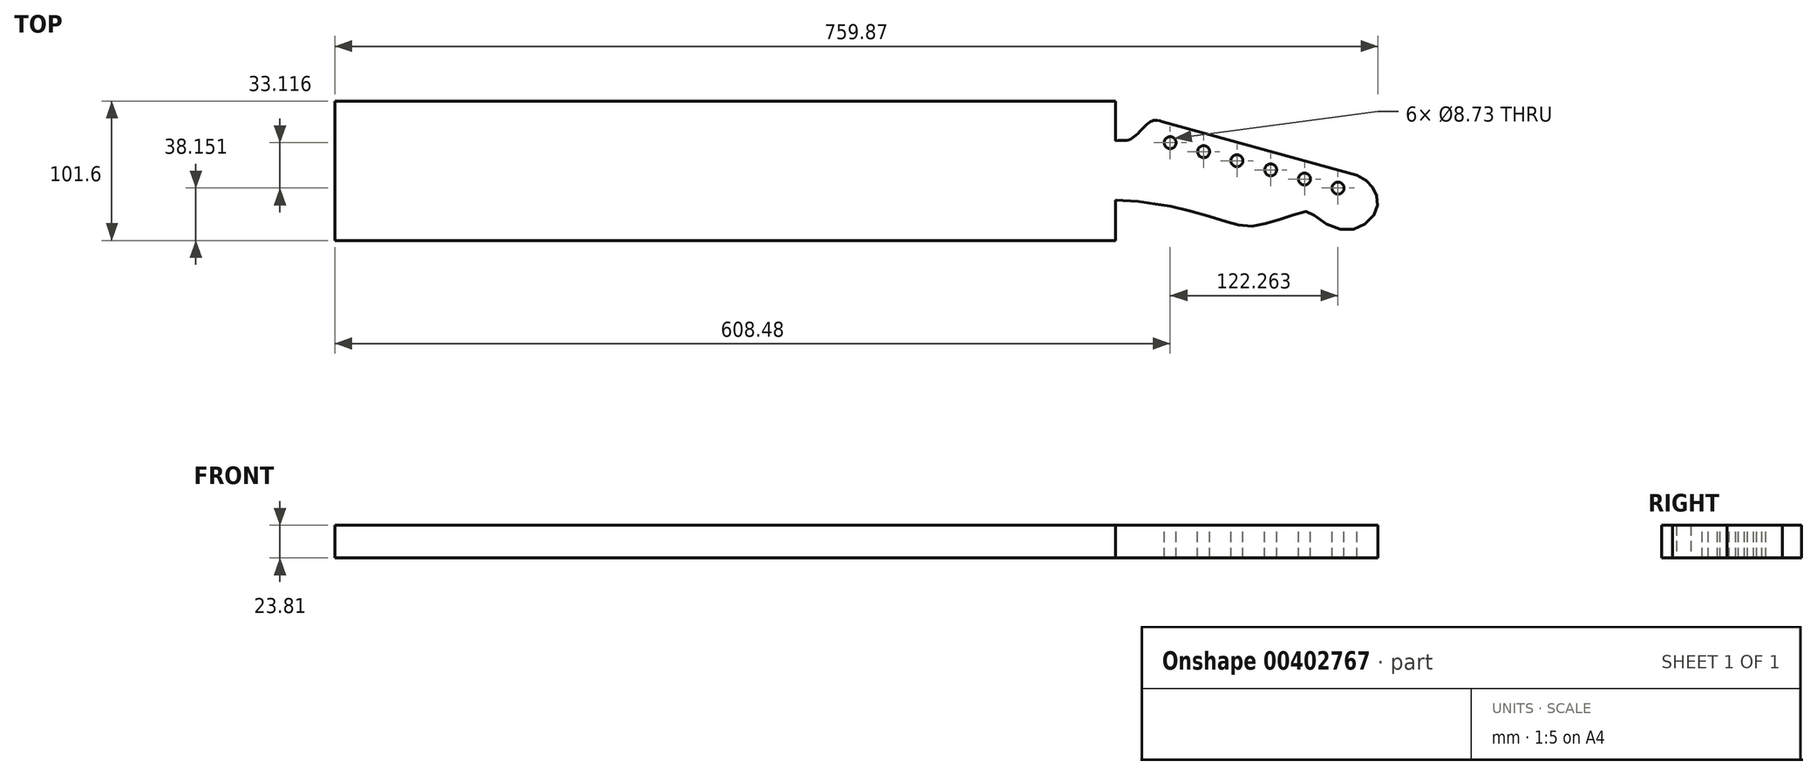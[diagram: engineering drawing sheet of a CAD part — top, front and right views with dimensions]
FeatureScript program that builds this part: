
annotation { "Feature Type Name" : "Feature", "Feature Type Description" : "" }
export const myFeature = defineFeature(function(context is Context, id is Id, definition is map)
    precondition{}
    {
        {
            var Q0;
            Q0=qCreatedBy(makeId("Top.planeOp"),FACE);
            var sketch = newSketch(context, id + "F0", { "sketchPlane" : qUnion([Q0])});
            skLineSegment(sketch, "E0", {"start": v(-323.85, 0) * mm, "end": v(323.85, 0) * mm, "construction": true});
            skLineSegment(sketch, "E1", {"start": v(323.85, 21.43) * mm, "end": v(323.85, -21.43) * mm, "construction": true});
            skLineSegment(sketch, "E2", {"start": v(323.85, 0) * mm, "end": v(327.03, 0) * mm, "construction": true});
            skLineSegment(sketch, "E3", {"start": v(327.03, 21.43) * mm, "end": v(327.03, -21.43) * mm, "construction": true});
            skSolve(sketch);
        }
        {
            var Q0;
            Q0=qCreatedBy(makeId("Top.planeOp"),FACE);
            var sketch = newSketch(context, id + "F1", { "sketchPlane" : qUnion([Q0])});
            skLineSegment(sketch, "E4.bottom", {"start": v(520.42, 50.8) * mm, "end": v(-241.58, 50.8) * mm});
            skLineSegment(sketch, "E4.top", {"start": v(520.42, -50.8) * mm, "end": v(-241.58, -50.8) * mm});
            skLineSegment(sketch, "E4.left", {"start": v(520.42, 50.8) * mm, "end": v(520.42, -50.8) * mm});
            skLineSegment(sketch, "E4.right", {"start": v(-241.58, 50.8) * mm, "end": v(-241.58, -50.8) * mm});
            skPoint(sketch, "E5", {"position": v(520.42, 0) * mm});
            skSolve(sketch);
        }
        {
            var Q0;
            Q0 = qSketchRegion(id + "F1", true);
            extrude(context, id + "F2", {"entities" : qUnion([Q0]), "oppositeDirection" : true, "depth" : 23.8 * mm});
        }
        {
            var Q0;
            Q0=qCreatedBy(makeId("Top.planeOp"),FACE);
            var sketch = newSketch(context, id + "F3", { "sketchPlane" : qUnion([Q0])});
            skLineSegment(sketch, "E6", {"start": v(325.44, 21.43) * mm, "end": v(325.44, -21.43) * mm});
            skCircle(sketch, "E7", {"center": v(366.9, 20.47) * mm, "radius": 4.37 * mm});
            skPoint(sketch, "E8", {"position": v(325.44, 0) * mm});
            skLineSegment(sketch, "E9", {"start": v(-178.02, 0) * mm, "end": v(520.42, 0) * mm, "construction": true});
            skPoint(sketch, "E10", {"position": v(361.08, 35.86) * mm});
            skPoint(sketch, "E11", {"position": v(503.05, -3.23) * mm});
            skLineSegment(sketch, "E12", {"start": v(361.08, 35.86) * mm, "end": v(503.05, -3.23) * mm});
            skCircle(sketch, "E13", {"center": v(489.16, -12.65) * mm, "radius": 4.37 * mm});
            skLineSegment(sketch, "E14", {"start": v(366.9, 20.47) * mm, "end": v(489.16, -12.65) * mm, "construction": true});
            skCircle(sketch, "E15", {"center": v(464.73, -6.03) * mm, "radius": 4.37 * mm});
            skCircle(sketch, "E16", {"center": v(440.11, 0.64) * mm, "radius": 4.37 * mm});
            skCircle(sketch, "E17", {"center": v(415.53, 7.3) * mm, "radius": 4.37 * mm});
            skCircle(sketch, "E18", {"center": v(391.26, 13.87) * mm, "radius": 4.37 * mm});
            skFitSpline(sketch, "E19", {"points": [v(325.44, 21.43) * mm, v(327.1, 21.9) * mm, v(333.07, 22.03) * mm, v(336.36, 22.34) * mm, v(339.35, 23.78) * mm, v(341.85, 25.84) * mm, v(345.43, 29.07) * mm, v(348.04, 31.8) * mm, v(350.96, 34.6) * mm, v(352.85, 35.86) * mm, v(354.59, 36.56) * mm, v(357, 36.8) * mm, v(361.08, 35.86) * mm], "startDerivative": vector(37.26, 13.78) * mm, "endDerivative": vector(36.1, -10.12) * mm});
            skFitSpline(sketch, "E20", {"points": [v(503.05, -3.23) * mm, v(506.37, -4.8) * mm, v(509.18, -6.58) * mm, v(511.22, -8.3) * mm, v(513.52, -10.68) * mm, v(514.8, -12.55) * mm, v(515.71, -14.1) * mm, v(516.9, -16.6) * mm, v(517.94, -20.39) * mm, v(518.28, -23.08) * mm, v(517.88, -25.45) * mm, v(517.12, -28.72) * mm, v(515.68, -31.71) * mm, v(513.48, -34.87) * mm, v(508.97, -38.7) * mm, v(505.91, -40.6) * mm, v(500.06, -42.62) * mm, v(494.92, -43) * mm, v(489.64, -42.33) * mm, v(482.92, -40.03) * mm, v(477, -36.51) * mm, v(471.92, -32.56) * mm, v(469.6, -30.94) * mm, v(466.93, -29.84) * mm, v(464.15, -29.84) * mm, v(459.7, -31.04) * mm, v(452.05, -33.78) * mm, v(445.7, -35.92) * mm, v(438.84, -37.9) * mm, v(434.66, -38.86) * mm, v(428.94, -40.12) * mm, v(423.1, -40.22) * mm, v(417.53, -39.46) * mm, v(414.25, -38.83) * mm, v(410.12, -37.73) * mm, v(401.68, -35.12) * mm, v(388.65, -31.03) * mm, v(378.38, -28.5) * mm, v(366.33, -25.67) * mm, v(359.59, -24.69) * mm, v(351.28, -23.36) * mm, v(341.71, -22.32) * mm, v(325.44, -21.43) * mm], "startDerivative": vector(168.4, -74.25) * mm, "endDerivative": vector(-412.17, 19.2) * mm});
            skLineSegment(sketch, "E21.0", {"start": v(520.42, 50.8) * mm, "end": v(-241.58, 50.8) * mm, "construction": true});
            skLineSegment(sketch, "E22.0", {"start": v(520.42, -50.8) * mm, "end": v(-241.58, -50.8) * mm, "construction": true});
            skLineSegment(sketch, "E23.0", {"start": v(520.42, 50.8) * mm, "end": v(520.42, -50.8) * mm, "construction": true});
            skPoint(sketch, "E24.0", {"position": v(327.03, 21.43) * mm});
            skLineSegment(sketch, "E25.bottom", {"start": v(327.1, 50.8) * mm, "end": v(520.42, 50.8) * mm});
            skLineSegment(sketch, "E25.top", {"start": v(327.1, -50.8) * mm, "end": v(520.42, -50.8) * mm});
            skLineSegment(sketch, "E25.left", {"start": v(327.1, 50.8) * mm, "end": v(327.1, -50.8) * mm});
            skLineSegment(sketch, "E25.right", {"start": v(520.42, 50.8) * mm, "end": v(520.42, -50.8) * mm});
            skSolve(sketch);
        }
        {
            var Q0;
            {var subQ1=sQuery(id+"F3.wireOp",EDGE,"E12");Q0=makeQuery(id+"F3.imprint","IMPRINT",FACE,{"disambiguationData":[TD([[makeQuery(id+"F3.imprint","IMPRINT",EDGE,{"derivedFrom":subQ1}),1.0]])]});}
            var Q1;
            Q1=makeQuery(id+"F3.imprint","IMPRINT",FACE,{"disambiguationData":[TD([[makeQuery(id+"F3.imprint","IMPRINT",EDGE,{"derivedFrom":sQuery(id+"F3.wireOp",EDGE,"E13")}),1.0]])]});
            var Q2;
            Q2=makeQuery(id+"F3.imprint","IMPRINT",FACE,{"disambiguationData":[TD([[makeQuery(id+"F3.imprint","IMPRINT",EDGE,{"derivedFrom":sQuery(id+"F3.wireOp",EDGE,"E15")}),1.0]])]});
            var Q3;
            Q3=makeQuery(id+"F3.imprint","IMPRINT",FACE,{"disambiguationData":[TD([[makeQuery(id+"F3.imprint","IMPRINT",EDGE,{"derivedFrom":sQuery(id+"F3.wireOp",EDGE,"E16")}),1.0]])]});
            var Q4;
            Q4=makeQuery(id+"F3.imprint","IMPRINT",FACE,{"disambiguationData":[TD([[makeQuery(id+"F3.imprint","IMPRINT",EDGE,{"derivedFrom":sQuery(id+"F3.wireOp",EDGE,"E17")}),1.0]])]});
            var Q5;
            Q5=makeQuery(id+"F3.imprint","IMPRINT",FACE,{"disambiguationData":[TD([[makeQuery(id+"F3.imprint","IMPRINT",EDGE,{"derivedFrom":sQuery(id+"F3.wireOp",EDGE,"E18")}),1.0]])]});
            var Q6;
            Q6=makeQuery(id+"F3.imprint","IMPRINT",FACE,{"disambiguationData":[TD([[makeQuery(id+"F3.imprint","IMPRINT",EDGE,{"derivedFrom":sQuery(id+"F3.wireOp",EDGE,"E7")}),1.0]])]});
            var Q7;
            Q7=makeQuery(id+"F2.opExtrude","CAP_FACE",FACE,{"disambiguationData":[OSD([sQuery(id+"F1.wireOp",EDGE,"E4.bottom"),sQuery(id+"F1.wireOp",EDGE,"E4.top"),sQuery(id+"F1.wireOp",EDGE,"E4.left"),sQuery(id+"F1.wireOp",EDGE,"E4.right")])],"isStart":false});
            extrude(context, id + "F4", {"entities" : qUnion([Q0, Q1, Q2, Q3, Q4, Q5, Q6, Q7]), "operationType" : NewBodyOperationType.REMOVE, "endBound" : BoundingType.THROUGH_ALL, "oppositeDirection" : true, "depth" : 25.4 * mm});
        }
    });
